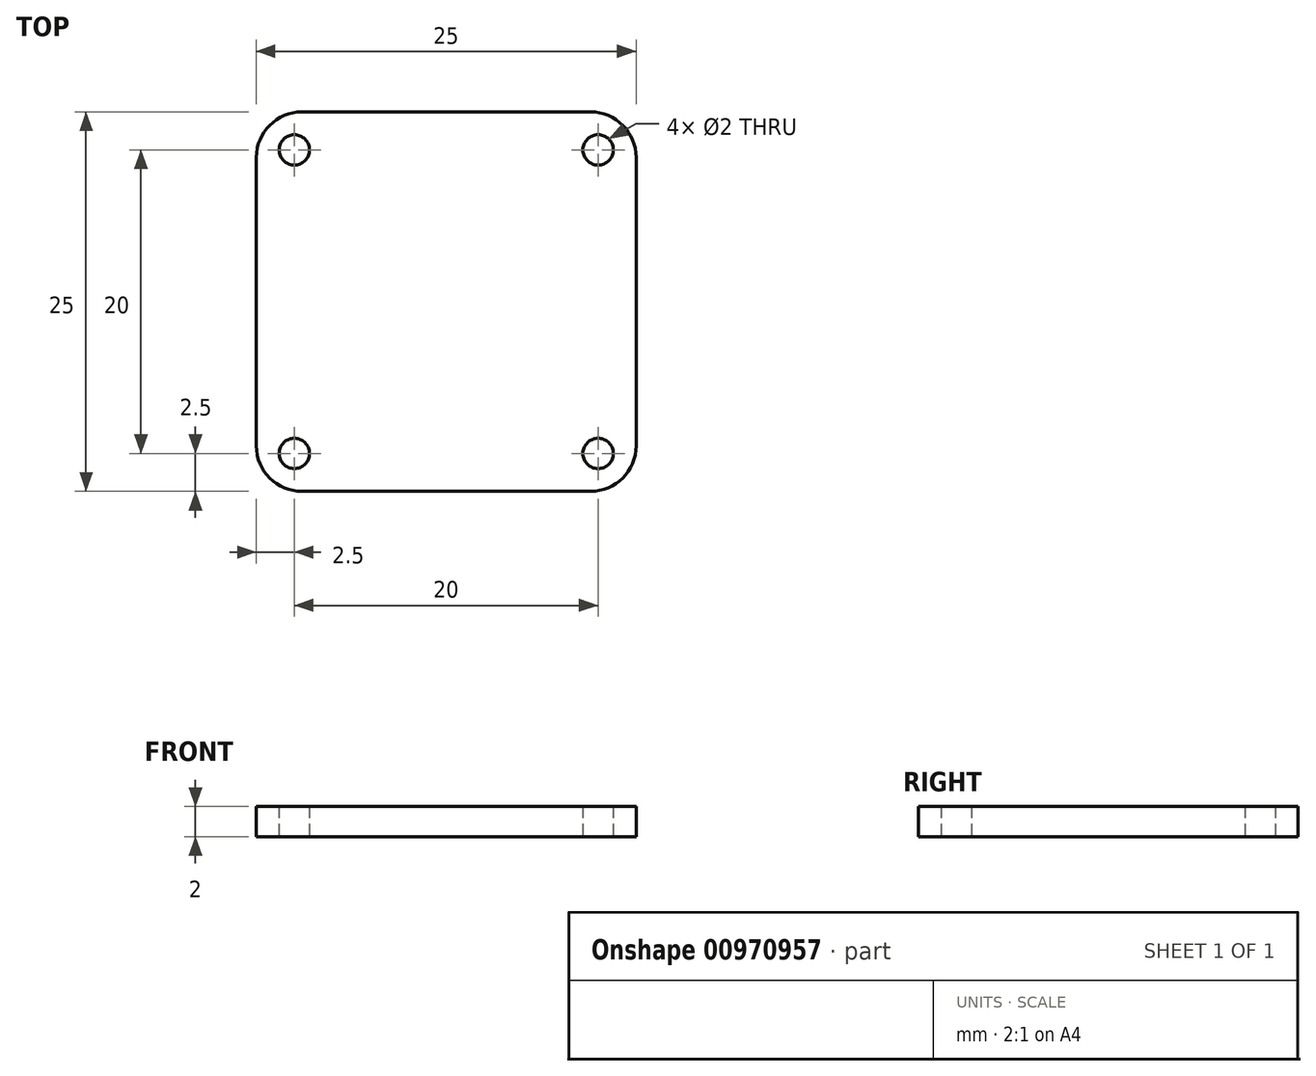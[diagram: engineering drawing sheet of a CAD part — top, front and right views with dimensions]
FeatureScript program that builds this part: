
annotation { "Feature Type Name" : "Feature", "Feature Type Description" : "" }
export const myFeature = defineFeature(function(context is Context, id is Id, definition is map)
    precondition{}
    {
        {
            var Q0;
            Q0=qCreatedBy(makeId("Top.planeOp"),FACE);
            var sketch = newSketch(context, id + "F0", { "sketchPlane" : qUnion([Q0])});
            skLineSegment(sketch, "E0.bottom", {"start": v(-10, 10) * mm, "end": v(10, 10) * mm, "construction": true});
            skLineSegment(sketch, "E0.top", {"start": v(-10, -10) * mm, "end": v(10, -10) * mm, "construction": true});
            skLineSegment(sketch, "E0.left", {"start": v(-10, 10) * mm, "end": v(-10, -10) * mm, "construction": true});
            skLineSegment(sketch, "E0.right", {"start": v(10, 10) * mm, "end": v(10, -10) * mm, "construction": true});
            skPoint(sketch, "E0.middle", {"position": v(0, 0) * mm});
            skLineSegment(sketch, "E1.bottom", {"start": v(-9.5, 12.5) * mm, "end": v(9.5, 12.5) * mm});
            skLineSegment(sketch, "E1.top", {"start": v(-9.5, -12.5) * mm, "end": v(9.5, -12.5) * mm});
            skLineSegment(sketch, "E1.left", {"start": v(-12.5, 9.5) * mm, "end": v(-12.5, -9.5) * mm});
            skLineSegment(sketch, "E1.right", {"start": v(12.5, 9.5) * mm, "end": v(12.5, -9.5) * mm});
            skCircle(sketch, "E2", {"center": v(-10, 10) * mm, "radius": 1 * mm});
            skCircle(sketch, "E3", {"center": v(10, 10) * mm, "radius": 1 * mm});
            skCircle(sketch, "E4", {"center": v(10, -10) * mm, "radius": 1 * mm});
            skCircle(sketch, "E5", {"center": v(-10, -10) * mm, "radius": 1 * mm});
            skPoint(sketch, "E6.visualSharp", {"position": v(-12.5, 12.5) * mm});
            skArc(sketch, "E6.filletArc", {"start": v(-9.5, 12.5) * mm, "mid": v(-11.62, 11.62) * mm, "end": v(-12.5, 9.5) * mm});
            skPoint(sketch, "E7.visualSharp", {"position": v(12.5, 12.5) * mm});
            skArc(sketch, "E7.filletArc", {"start": v(12.5, 9.5) * mm, "mid": v(11.62, 11.62) * mm, "end": v(9.5, 12.5) * mm});
            skPoint(sketch, "E8.visualSharp", {"position": v(12.5, -12.5) * mm});
            skArc(sketch, "E8.filletArc", {"start": v(9.5, -12.5) * mm, "mid": v(11.62, -11.62) * mm, "end": v(12.5, -9.5) * mm});
            skPoint(sketch, "E9.visualSharp", {"position": v(-12.5, -12.5) * mm});
            skArc(sketch, "E9.filletArc", {"start": v(-12.5, -9.5) * mm, "mid": v(-11.62, -11.62) * mm, "end": v(-9.5, -12.5) * mm});
            skSolve(sketch);
        }
        {
            var Q0;
            Q0=makeQuery(id+"F0.imprint","IMPRINT",FACE,{"disambiguationData":[TD([[makeQuery(id+"F0.imprint","IMPRINT",EDGE,{"derivedFrom":sQuery(id+"F0.wireOp",EDGE,"E1.bottom")}),-1.0]])]});
            extrude(context, id + "F1", {"entities" : qUnion([Q0]), "depth" : 2 * mm, "offsetDistance" : 25 * mm});
        }
    });
